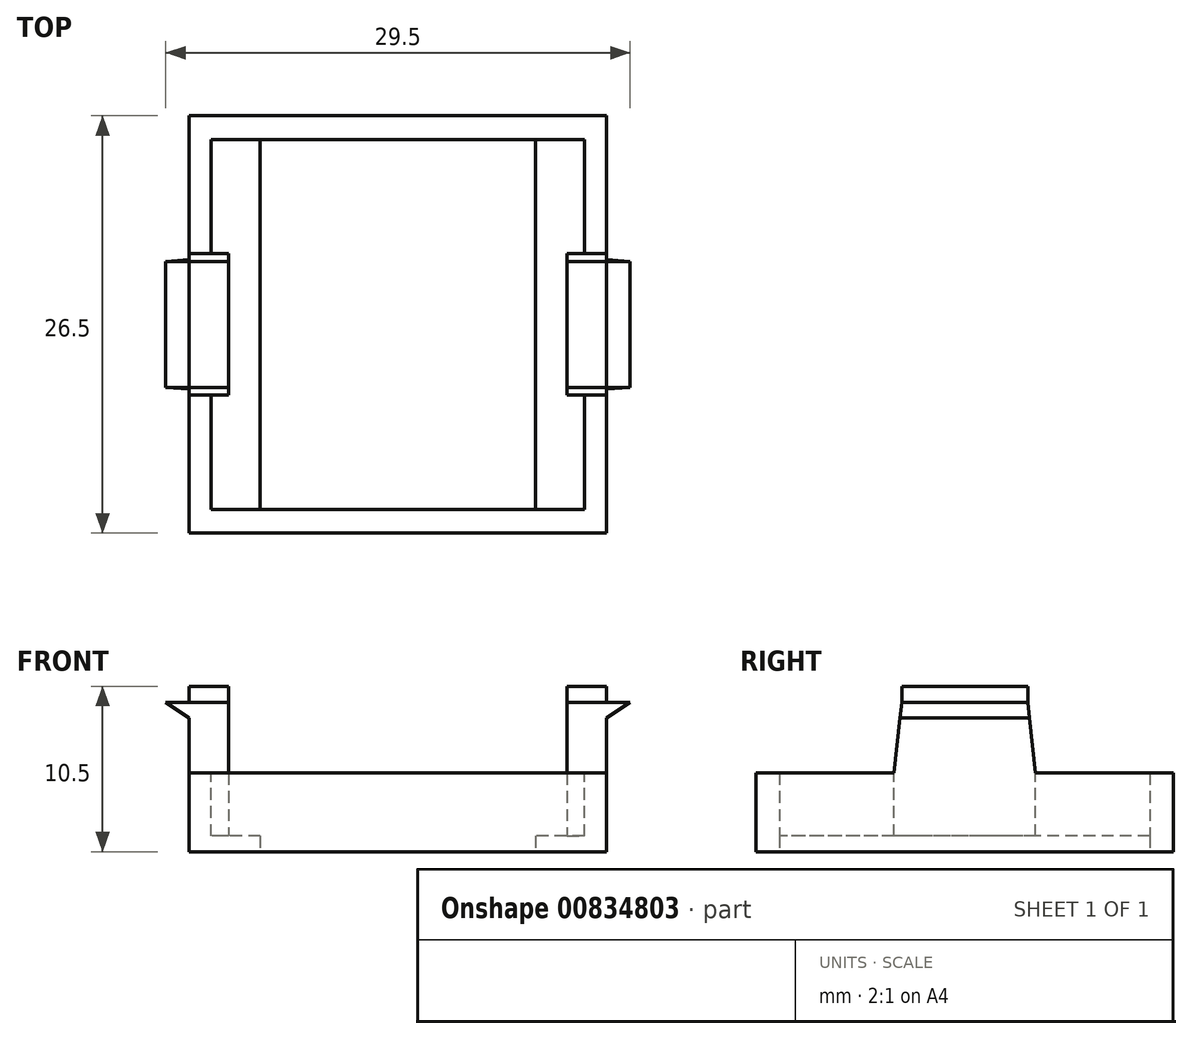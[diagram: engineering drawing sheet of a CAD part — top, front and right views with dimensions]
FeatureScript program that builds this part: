
annotation { "Feature Type Name" : "Feature", "Feature Type Description" : "" }
export const myFeature = defineFeature(function(context is Context, id is Id, definition is map)
    precondition{}
    {
        {
            var Q0;
            Q0=qCreatedBy(makeId("Top.planeOp"),FACE);
            var sketch = newSketch(context, id + "F0", { "sketchPlane" : qUnion([Q0])});
            skLineSegment(sketch, "E0.bottom", {"start": v(13.25, 13.25) * mm, "end": v(-13.25, 13.25) * mm});
            skLineSegment(sketch, "E0.top", {"start": v(13.25, -13.25) * mm, "end": v(-13.25, -13.25) * mm});
            skLineSegment(sketch, "E0.left", {"start": v(13.25, 13.25) * mm, "end": v(13.25, -13.25) * mm});
            skLineSegment(sketch, "E0.right", {"start": v(-13.25, 13.25) * mm, "end": v(-13.25, -13.25) * mm});
            skPoint(sketch, "E0.middle", {"position": v(0, 0) * mm});
            skLineSegment(sketch, "E1.bottom", {"start": v(11.85, 11.75) * mm, "end": v(-11.85, 11.75) * mm});
            skLineSegment(sketch, "E1.top", {"start": v(11.85, -11.75) * mm, "end": v(-11.85, -11.75) * mm});
            skLineSegment(sketch, "E1.left", {"start": v(11.85, 11.75) * mm, "end": v(11.85, -11.75) * mm});
            skLineSegment(sketch, "E1.right", {"start": v(-11.85, 11.75) * mm, "end": v(-11.85, -11.75) * mm});
            skSolve(sketch);
        }
        {
            var Q0;
            Q0 = qSketchRegion(id + "F0", true);
            extrude(context, id + "F1", {"entities" : qUnion([Q0]), "depth" : 5 * mm, "offsetDistance" : 25 * mm});
        }
        {
            var Q0;
            Q0=qCreatedBy(makeId("Top.planeOp"),FACE);
            var sketch = newSketch(context, id + "F2", { "sketchPlane" : qUnion([Q0])});
            skLineSegment(sketch, "E2.bottom", {"start": v(-13.25, 13.25) * mm, "end": v(13.25, 13.25) * mm});
            skLineSegment(sketch, "E2.top", {"start": v(-13.25, -13.25) * mm, "end": v(13.25, -13.25) * mm});
            skLineSegment(sketch, "E2.left", {"start": v(-13.25, 13.25) * mm, "end": v(-13.25, -13.25) * mm});
            skLineSegment(sketch, "E2.right", {"start": v(13.25, 13.25) * mm, "end": v(13.25, -13.25) * mm});
            skPoint(sketch, "E2.middle", {"position": v(0, 0) * mm});
            skLineSegment(sketch, "E3.bottom", {"start": v(8.75, 11.75) * mm, "end": v(-8.75, 11.75) * mm});
            skLineSegment(sketch, "E3.top", {"start": v(8.75, -11.75) * mm, "end": v(-8.75, -11.75) * mm});
            skLineSegment(sketch, "E3.left", {"start": v(8.75, 11.75) * mm, "end": v(8.75, -11.75) * mm});
            skLineSegment(sketch, "E3.right", {"start": v(-8.75, 11.75) * mm, "end": v(-8.75, -11.75) * mm});
            skSolve(sketch);
        }
        {
            var Q0;
            Q0 = qSketchRegion(id + "F2", true);
            extrude(context, id + "F3", {"entities" : qUnion([Q0]), "operationType" : NewBodyOperationType.ADD, "depth" : 1 * mm, "offsetDistance" : 25 * mm});
        }
        {
            var Q0;
            Q0=makeQuery(id+"F1.opExtrude","SWEPT_FACE",FACE,{"disambiguationData":[OSD([sQuery(id+"F0.wireOp",EDGE,"E0.right")])]});
            var sketch = newSketch(context, id + "F4", { "sketchPlane" : qUnion([Q0])});
            skLineSegment(sketch, "E4", {"start": v(0, 5) * mm, "end": v(-4.5, 5) * mm});
            skLineSegment(sketch, "E5", {"start": v(-4.5, 5) * mm, "end": v(-4, 9.5) * mm});
            skLineSegment(sketch, "E6", {"start": v(-4, 9.5) * mm, "end": v(0, 9.5) * mm});
            skLineSegment(sketch, "E7", {"start": v(0, 9.5) * mm, "end": v(0, 5) * mm});
            skLineSegment(sketch, "E8.MirrorCS", {"start": v(4, 9.5) * mm, "end": v(0, 9.5) * mm});
            skLineSegment(sketch, "E9.MirrorCS", {"start": v(4.5, 5) * mm, "end": v(4, 9.5) * mm});
            skLineSegment(sketch, "E10.MirrorCS", {"start": v(0, 5) * mm, "end": v(4.5, 5) * mm});
            skLineSegment(sketch, "E11", {"start": v(-4, 9.5) * mm, "end": v(-4, 10.5) * mm});
            skLineSegment(sketch, "E12", {"start": v(-4, 10.5) * mm, "end": v(4, 10.5) * mm});
            skLineSegment(sketch, "E13", {"start": v(4, 10.5) * mm, "end": v(4, 9.5) * mm});
            skLineSegment(sketch, "E14.bottom", {"start": v(-4.5, 5) * mm, "end": v(4.5, 5) * mm});
            skLineSegment(sketch, "E14.top", {"start": v(-4.5, 0) * mm, "end": v(4.5, 0) * mm});
            skLineSegment(sketch, "E14.left", {"start": v(-4.5, 5) * mm, "end": v(-4.5, 0) * mm});
            skLineSegment(sketch, "E14.right", {"start": v(4.5, 5) * mm, "end": v(4.5, 0) * mm});
            skSolve(sketch);
        }
        {
            var Q0;
            Q0 = qSketchRegion(id + "F4", true);
            extrude(context, id + "F5", {"entities" : qUnion([Q0]), "operationType" : NewBodyOperationType.ADD, "oppositeDirection" : true, "depth" : 2.5 * mm, "offsetDistance" : 25 * mm});
        }
        {
            var Q0;
            Q0=makeQuery(id+"F5.boolean.opBoolean","MERGE",FACE,{"derivedFrom":[makeQuery(id+"F1.opExtrude","SWEPT_FACE",FACE,{"disambiguationData":[OSD([sQuery(id+"F0.wireOp",EDGE,"E0.right")])]}),makeQuery(id+"F5.opExtrude","CAP_FACE",FACE,{"disambiguationData":[OSD([sQuery(id+"F4.wireOp",EDGE,"E4"),sQuery(id+"F4.wireOp",EDGE,"E5"),sQuery(id+"F4.wireOp",EDGE,"E6"),sQuery(id+"F4.wireOp",EDGE,"E8.MirrorCS"),sQuery(id+"F4.wireOp",EDGE,"E9.MirrorCS"),sQuery(id+"F4.wireOp",EDGE,"E10.MirrorCS")])],"isStart":true})]});
            var sketch = newSketch(context, id + "F6", { "sketchPlane" : qUnion([Q0])});
            skLineSegment(sketch, "E15", {"start": v(-4.11, 8.5) * mm, "end": v(-4, 9.5) * mm});
            skLineSegment(sketch, "E16", {"start": v(-4, 9.5) * mm, "end": v(4, 9.5) * mm});
            skLineSegment(sketch, "E17", {"start": v(4, 9.5) * mm, "end": v(4.11, 8.5) * mm});
            skLineSegment(sketch, "E18", {"start": v(4.11, 8.5) * mm, "end": v(-4.11, 8.5) * mm});
            skLineSegment(sketch, "E19.bottom", {"start": v(-4, 9.5) * mm, "end": v(-4, 9.5) * mm});
            skLineSegment(sketch, "E19.top", {"start": v(-4, 10.5) * mm, "end": v(-4, 10.5) * mm});
            skLineSegment(sketch, "E19.left", {"start": v(-4, 9.5) * mm, "end": v(-4, 10.5) * mm});
            skLineSegment(sketch, "E19.right", {"start": v(-4, 9.5) * mm, "end": v(-4, 10.5) * mm});
            skLineSegment(sketch, "E20.bottom", {"start": v(4, 10.5) * mm, "end": v(4, 10.5) * mm});
            skLineSegment(sketch, "E20.top", {"start": v(4, 9.5) * mm, "end": v(4, 9.5) * mm});
            skLineSegment(sketch, "E20.left", {"start": v(4, 10.5) * mm, "end": v(4, 9.5) * mm});
            skLineSegment(sketch, "E20.right", {"start": v(4, 10.5) * mm, "end": v(4, 9.5) * mm});
            skSolve(sketch);
        }
        {
            var Q0;
            Q0 = qSketchRegion(id + "F6", true);
            var Q1;
            Q1=makeQuery(id+"F6.imprint","IMPRINT",FACE,{"disambiguationData":[TD([[makeQuery(id+"F6.imprint","IMPRINT",EDGE,{"derivedFrom":sQuery(id+"F6.wireOp",EDGE,"E19.right")}),-1.0]])]});
            extrude(context, id + "F7", {"entities" : qUnion([Q0, Q1]), "operationType" : NewBodyOperationType.ADD, "depth" : 1.5 * mm, "offsetDistance" : 25 * mm});
        }
        {
            var Q0;
            Q0=qCreatedBy(makeId("Front.planeOp"),FACE);
            var sketch = newSketch(context, id + "F8", { "sketchPlane" : qUnion([Q0])});
            skLineSegment(sketch, "E21", {"start": v(-13.25, 8.5) * mm, "end": v(-14.75, 9.5) * mm});
            skLineSegment(sketch, "E22", {"start": v(-14.75, 9.5) * mm, "end": v(-14.75, 8.5) * mm});
            skLineSegment(sketch, "E23", {"start": v(-14.75, 8.5) * mm, "end": v(-13.25, 8.5) * mm});
            skLineSegment(sketch, "E24", {"start": v(-14.75, 9.5) * mm, "end": v(-13.25, 10.5) * mm});
            skLineSegment(sketch, "E25", {"start": v(-13.25, 10.5) * mm, "end": v(-14.75, 10.5) * mm});
            skLineSegment(sketch, "E26", {"start": v(-14.75, 10.5) * mm, "end": v(-14.75, 9.5) * mm});
            skSolve(sketch);
        }
        {
            var Q0;
            Q0 = qSketchRegion(id + "F8", true);
            extrude(context, id + "F9", {"entities" : qUnion([Q0]), "operationType" : NewBodyOperationType.REMOVE, "depth" : 25 * mm, "offsetDistance" : 25 * mm, "hasSecondDirection" : true, "secondDirectionOppositeDirection" : true, "secondDirectionDepth" : 25 * mm});
        }
        {
            var Q0;
            Q0=makeQuery(id+"F1.opExtrude","SWEPT_BODY",BODY,{"disambiguationData":[OSD([sQuery(id+"F0.wireOp",EDGE,"E0.bottom"),sQuery(id+"F0.wireOp",EDGE,"E0.top"),sQuery(id+"F0.wireOp",EDGE,"E0.left"),sQuery(id+"F0.wireOp",EDGE,"E0.right"),sQuery(id+"F0.wireOp",EDGE,"E1.bottom"),sQuery(id+"F0.wireOp",EDGE,"E1.top"),sQuery(id+"F0.wireOp",EDGE,"E1.left"),sQuery(id+"F0.wireOp",EDGE,"E1.right")])]});
            var Q1;
            Q1=qCreatedBy(makeId("Right.planeOp"),FACE);
            mirror(context, id + "F10", {"operationType" : NewBodyOperationType.ADD, "entities" : qUnion([Q0]), "mirrorPlane" : qUnion([Q1])});
        }
    });
